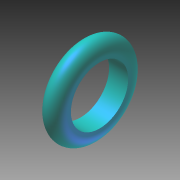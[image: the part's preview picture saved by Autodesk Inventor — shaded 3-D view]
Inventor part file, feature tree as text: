
AUTODESK INVENTOR PART (.ipt)
format: ipt  version: 2012 (Build 160160000, 160)  size: 159,232 bytes
history: native  units: in
note: dims shown in document units (in); Inventor stores cm internally (conversion verified against a paired STEP export)
features: revolve x1, sketch x1
ambient origin geometry x8: Origin, YZ Plane, XZ Plane, XY Plane, X Axis, Y Axis, Z Axis, Center Point
bodies: Solid1 (feature_tree)
feature tree (2):
  revolve  "Revolution1"  [1 undecoded]
  sketch  "Sketch1"  dims[d0=0.125in d1=0.75in d2=1.125in d3=0.5in d4=0.375in d5=0.75in d6=90.0deg]
note: 1 required parameter value undecoded (feature->parameter linkage not recoverable at this tier; creation-order binding heuristic only, values carry confidence <= 0.55)
